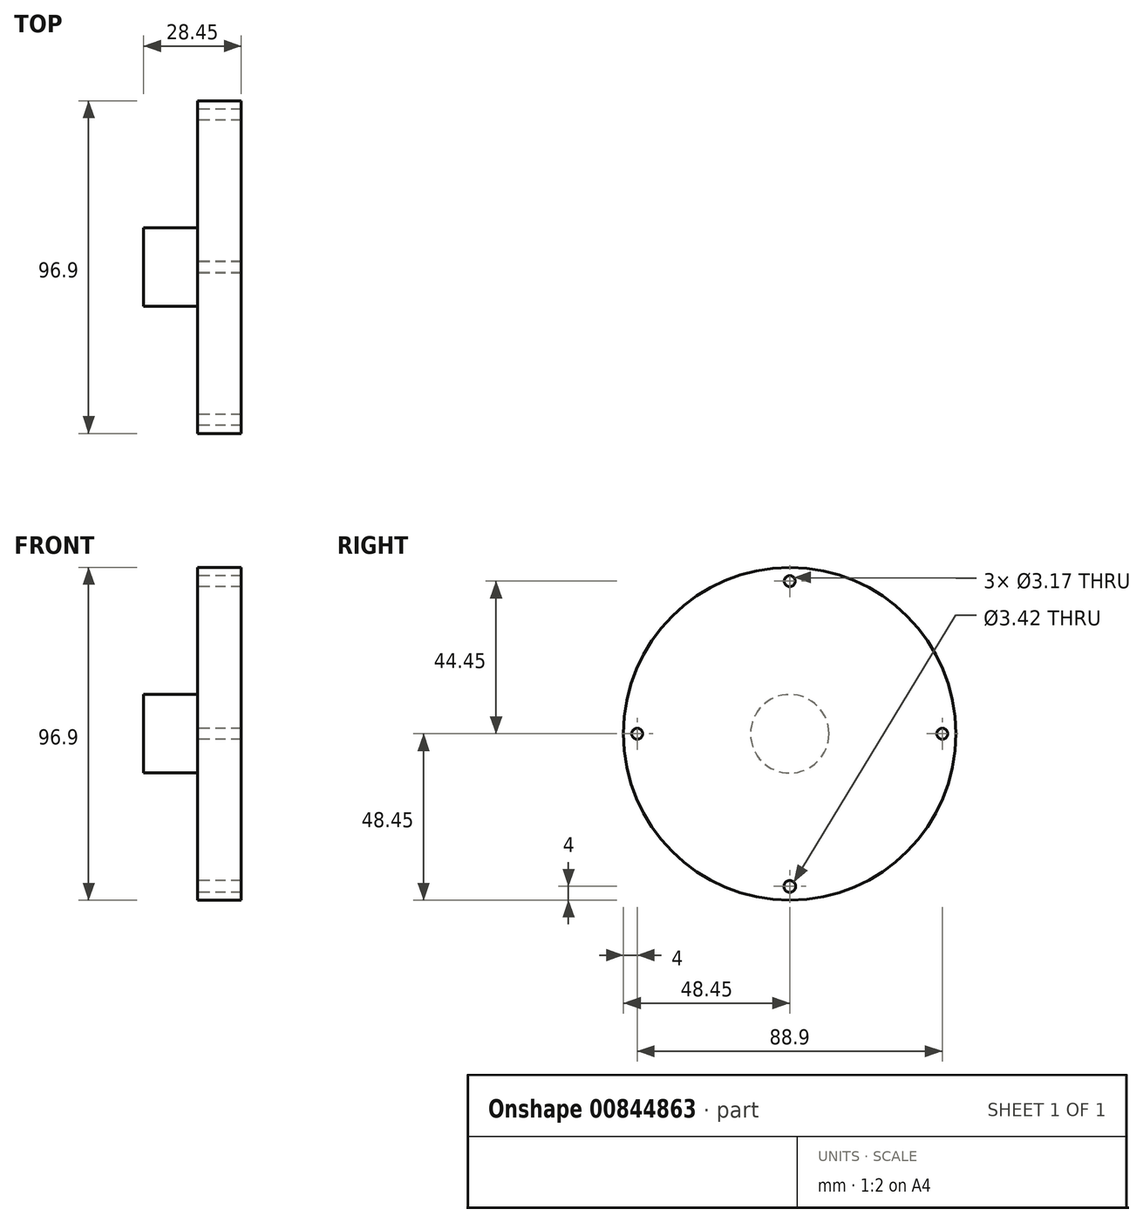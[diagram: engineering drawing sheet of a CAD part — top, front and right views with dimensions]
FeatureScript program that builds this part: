
annotation { "Feature Type Name" : "Feature", "Feature Type Description" : "" }
export const myFeature = defineFeature(function(context is Context, id is Id, definition is map)
    precondition{}
    {
        {
            var Q0;
            Q0=qCreatedBy(makeId("Right.planeOp"),FACE);
            var sketch = newSketch(context, id + "F0", { "sketchPlane" : qUnion([Q0])});
            skCircle(sketch, "E0", {"center": v(0, 0) * mm, "radius": 48.45 * mm});
            skSolve(sketch);
        }
        {
            var Q0;
            Q0=makeQuery(id+"F0.imprint","IMPRINT",FACE,{"disambiguationData":[TD([[makeQuery(id+"F0.imprint","IMPRINT",EDGE,{"derivedFrom":sQuery(id+"F0.wireOp",EDGE,"E0")}),1.0]])]});
            extrude(context, id + "F1", {"entities" : qUnion([Q0]), "depth" : 12.7 * mm, "offsetDistance" : 25.4 * mm});
        }
        {
            var Q0;
            Q0=makeQuery(id+"F1.opExtrude","CAP_FACE",FACE,{"disambiguationData":[OSD([sQuery(id+"F0.wireOp",EDGE,"E0")])],"isStart":true});
            var sketch = newSketch(context, id + "F2", { "sketchPlane" : qUnion([Q0])});
            skCircle(sketch, "E1", {"center": v(0, 0) * mm, "radius": 11.43 * mm});
            skSolve(sketch);
        }
        {
            var Q0;
            Q0 = qSketchRegion(id + "F2", true);
            var Q1;
            Q1=sQuery(id+"F2.wireOp",EDGE,"E1");
            extrude(context, id + "F3", {"entities" : qUnion([Q0]), "operationType" : NewBodyOperationType.ADD, "surfaceEntities" : qUnion([Q1]), "depth" : 15.75 * mm, "offsetDistance" : 25.4 * mm});
        }
        {
            var Q0;
            Q0=makeQuery(id+"F1.opExtrude","CAP_FACE",FACE,{"disambiguationData":[OSD([sQuery(id+"F0.wireOp",EDGE,"E0")])],"isStart":true});
            var sketch = newSketch(context, id + "F4", { "sketchPlane" : qUnion([Q0])});
            skCircle(sketch, "E2", {"center": v(0, 44.45) * mm, "radius": 1.59 * mm});
            skCircle(sketch, "E3", {"center": v(0, -44.45) * mm, "radius": 1.71 * mm});
            skCircle(sketch, "E4", {"center": v(44.45, 0) * mm, "radius": 1.59 * mm});
            skCircle(sketch, "E5", {"center": v(-44.45, 0) * mm, "radius": 1.59 * mm});
            skSolve(sketch);
        }
        {
            var Q0;
            Q0 = qSketchRegion(id + "F4", true);
            extrude(context, id + "F5", {"entities" : qUnion([Q0]), "operationType" : NewBodyOperationType.REMOVE, "oppositeDirection" : true, "depth" : 12.7 * mm, "offsetDistance" : 25.4 * mm});
        }
    });
